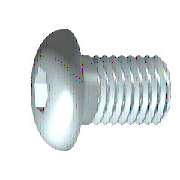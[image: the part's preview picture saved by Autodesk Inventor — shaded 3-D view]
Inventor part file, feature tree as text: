
AUTODESK INVENTOR PART (.ipt)
format: ipt  version: 2015 (Build 190159000, 159)  size: 200,704 bytes
history: native  units: mm (DEFAULTED — no unit token found)
features: sketch x2, extrude x1, plane x1, fillet x1
ambient origin geometry x7: Origin, YZ Plane, XY Plane, X Axis, Y Axis, Z Axis, Center Point
bodies: Solid1 (feature_tree), Body (feature_tree)
feature tree (5):
  extrude  "Slot"  Depth=1.8542mm
  plane  "Work Plane1"
  fillet  "Fillet2"  Radius=1.8542mm
  sketch  "Sketch1"  dims[d1=6.34726mm d2=1.59014mm d3=1.8542mm]
  sketch  "Sketch2"  dims[d4=1.1176mm d5=60.0deg d6=3.5052mm d7=3.5052mm d8=2.287693mm d9=6.6548mm d10=90.0deg d11=10.0mm d12=0.0mm d13=6.34726mm d14=0.0mm d15=0.486918mm d16=0.486918mm d17=1.6002mm d19=0.0mm d26=7.9375mm d27=45.0deg d28=0.0mm d29=0.0mm d30=0.1mm]
